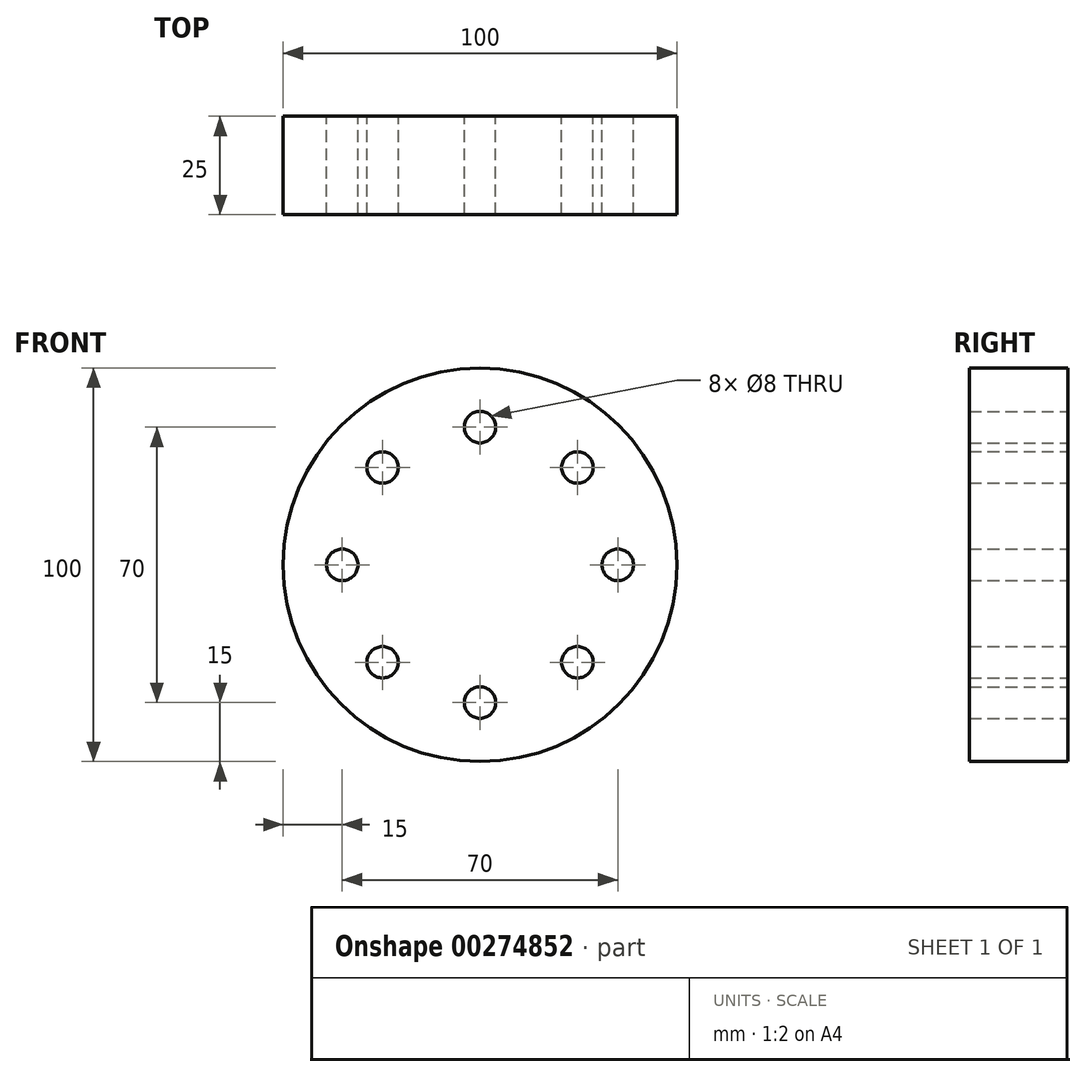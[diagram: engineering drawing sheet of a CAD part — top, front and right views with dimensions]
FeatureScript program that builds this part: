
annotation { "Feature Type Name" : "Feature", "Feature Type Description" : "" }
export const myFeature = defineFeature(function(context is Context, id is Id, definition is map)
    precondition{}
    {
        {
            var Q0;
            Q0=qCreatedBy(makeId("Front.planeOp"),FACE);
            var sketch = newSketch(context, id + "F0", { "sketchPlane" : qUnion([Q0])});
            skCircle(sketch, "E0", {"center": v(0, 0) * mm, "radius": 50 * mm});
            skCircle(sketch, "E1", {"center": v(-35, 0) * mm, "radius": 4 * mm});
            skCircle(sketch, "E2.1.0", {"center": v(-24.75, -24.75) * mm, "radius": 4 * mm});
            skCircle(sketch, "E2.2.0", {"center": v(0, -35) * mm, "radius": 4 * mm});
            skCircle(sketch, "E3.1.3.0", {"center": v(24.75, -24.75) * mm, "radius": 4 * mm});
            skCircle(sketch, "E3.1.4.0", {"center": v(35, 0) * mm, "radius": 4 * mm});
            skCircle(sketch, "E3.1.5.0", {"center": v(24.75, 24.75) * mm, "radius": 4 * mm});
            skCircle(sketch, "E3.1.6.0", {"center": v(0, 35) * mm, "radius": 4 * mm});
            skCircle(sketch, "E3.1.7.0", {"center": v(-24.75, 24.75) * mm, "radius": 4 * mm});
            skSolve(sketch);
        }
        {
            var Q0;
            Q0=makeQuery(id+"F0.imprint","IMPRINT",FACE,{"disambiguationData":[TD([[makeQuery(id+"F0.imprint","IMPRINT",EDGE,{"derivedFrom":sQuery(id+"F0.wireOp",EDGE,"E0")}),1.0]])]});
            extrude(context, id + "F1", {"entities" : qUnion([Q0]), "depth" : 25 * mm});
        }
    });
